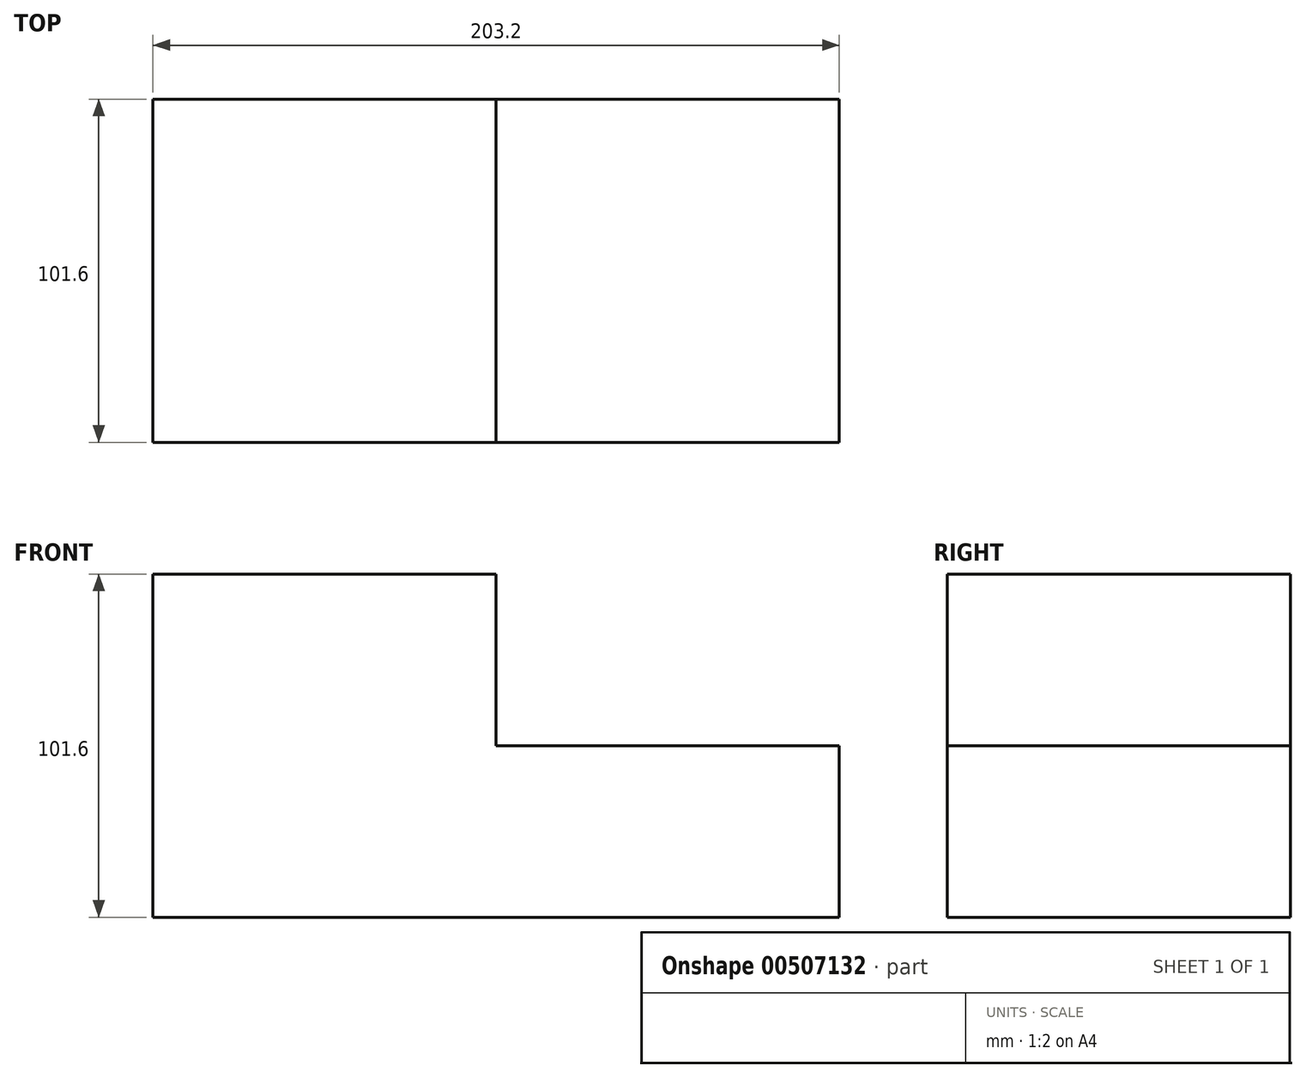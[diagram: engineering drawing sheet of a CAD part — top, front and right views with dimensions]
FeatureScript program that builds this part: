
annotation { "Feature Type Name" : "Feature", "Feature Type Description" : "" }
export const myFeature = defineFeature(function(context is Context, id is Id, definition is map)
    precondition{}
    {
        {
            var Q0;
            Q0=qCreatedBy(makeId("Front.planeOp"),FACE);
            var sketch = newSketch(context, id + "F0", { "sketchPlane" : qUnion([Q0])});
            skLineSegment(sketch, "E0.bottom", {"start": v(101.6, -50.8) * mm, "end": v(-101.6, -50.8) * mm});
            skLineSegment(sketch, "E0.top", {"start": v(101.6, 50.8) * mm, "end": v(-101.6, 50.8) * mm});
            skLineSegment(sketch, "E0.left", {"start": v(101.6, -50.8) * mm, "end": v(101.6, 50.8) * mm});
            skLineSegment(sketch, "E0.right", {"start": v(-101.6, -50.8) * mm, "end": v(-101.6, 50.8) * mm});
            skPoint(sketch, "E0.middle", {"position": v(0, 0) * mm});
            skLineSegment(sketch, "E1", {"start": v(0, 0) * mm, "end": v(0, 50.8) * mm});
            skLineSegment(sketch, "E2", {"start": v(0, 0) * mm, "end": v(101.6, 0) * mm});
            skSolve(sketch);
        }
        {
            var Q0;
            {var subQ1=sQuery(id+"F0.wireOp",EDGE,"E0.bottom");Q0=makeQuery(id+"F0.imprint","IMPRINT",FACE,{"disambiguationData":[TD([[makeQuery(id+"F0.imprint","IMPRINT",EDGE,{"derivedFrom":subQ1}),-1.0]])]});}
            extrude(context, id + "F1", {"entities" : qUnion([Q0]), "depth" : 101.6 * mm});
        }
    });
